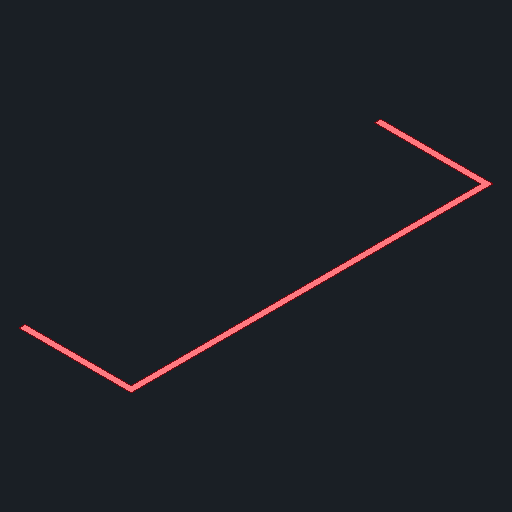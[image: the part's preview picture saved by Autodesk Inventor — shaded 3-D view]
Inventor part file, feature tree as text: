
AUTODESK INVENTOR PART (.ipt)
format: ipt  version: 2024 (Build 280153000, 153)  size: 83,968 bytes
history: native  units: in
note: dims shown in document units (in); Inventor stores cm internally (conversion verified against a paired STEP export)
features: extrude x1
ambient origin geometry x8: Origin, YZ Plane, XZ Plane, XY Plane, X Axis, Y Axis, Z Axis, Center Point
bodies: Solid1 (feature_tree)
feature tree (1):
  extrude  "Extrude-Thin1"  [1 undecoded]
note: 1 required parameter value undecoded (feature->parameter linkage not recoverable at this tier; creation-order binding heuristic only, values carry confidence <= 0.55)
